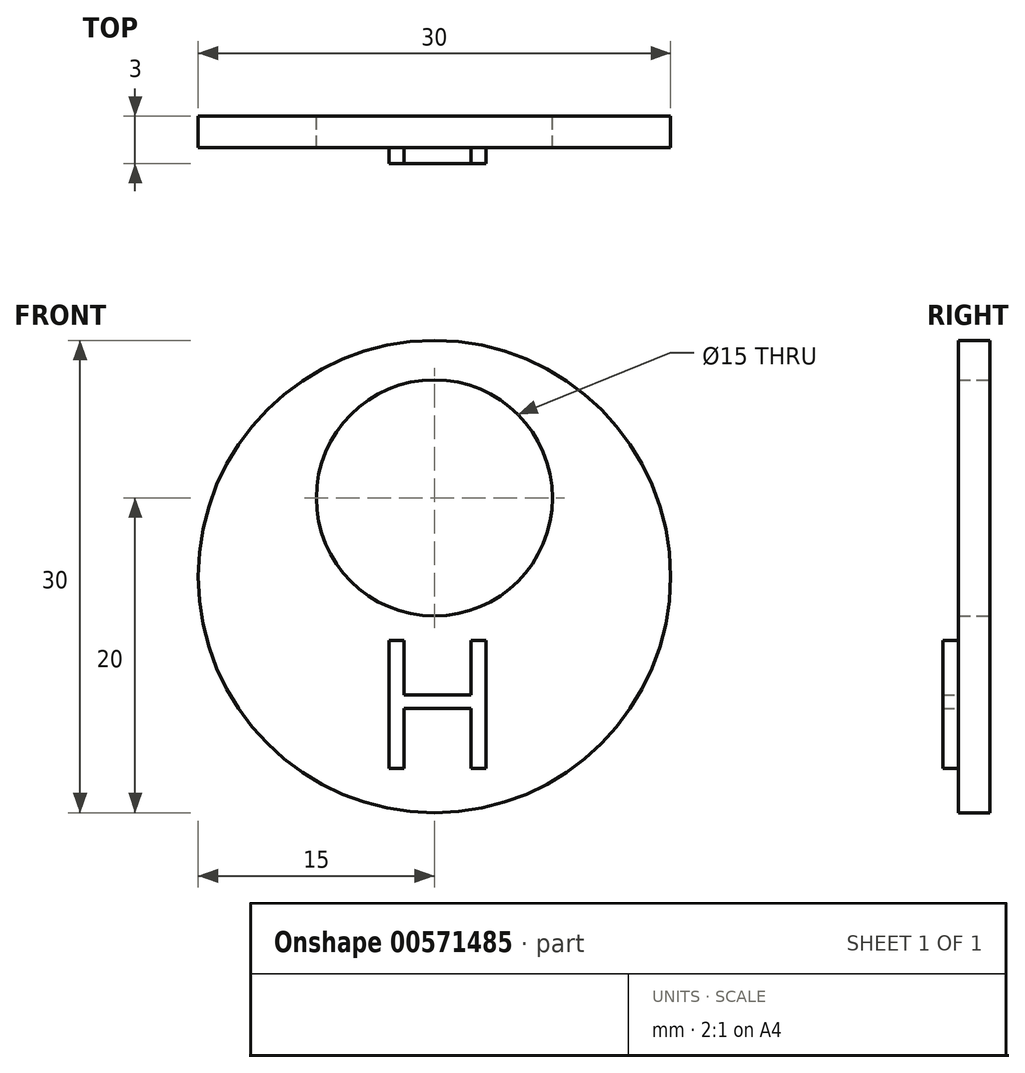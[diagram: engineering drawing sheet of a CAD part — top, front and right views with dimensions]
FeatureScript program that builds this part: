
annotation { "Feature Type Name" : "Feature", "Feature Type Description" : "" }
export const myFeature = defineFeature(function(context is Context, id is Id, definition is map)
    precondition{}
    {
        {
            var Q0;
            Q0=qCreatedBy(makeId("Front.planeOp"),FACE);
            var sketch = newSketch(context, id + "F0", { "sketchPlane" : qUnion([Q0])});
            skCircle(sketch, "E0", {"center": v(0, 0) * mm, "radius": 15 * mm});
            skPoint(sketch, "E1", {"position": v(0, 5) * mm});
            skCircle(sketch, "E2", {"center": v(0, 5) * mm, "radius": 7.5 * mm});
            skSolve(sketch);
        }
        {
            var Q0;
            Q0=makeQuery(id+"F0.imprint","IMPRINT",FACE,{"disambiguationData":[TD([[makeQuery(id+"F0.imprint","IMPRINT",EDGE,{"derivedFrom":sQuery(id+"F0.wireOp",EDGE,"E0")}),1.0]])]});
            extrude(context, id + "F1", {"entities" : qUnion([Q0]), "depth" : 2 * mm});
        }
        {
            var Q0;
            Q0=makeQuery(id+"F1.opExtrude","CAP_FACE",FACE,{"disambiguationData":[OSD([sQuery(id+"F0.wireOp",EDGE,"E0"),sQuery(id+"F0.wireOp",EDGE,"E2")])],"isStart":false});
            var sketch = newSketch(context, id + "F2", { "sketchPlane" : qUnion([Q0])});
            skText(sketch, "E3", { "text": "H", "fontName": "OpenSans-Regular.ttf"});
            const initialGuessF2  = {"E3": [-0.004, -0.01217, 1, 0, 0.00817]};
            skSetInitialGuess(sketch, initialGuessF2);
            skSolve(sketch);
        }
        {
            var Q0;
            Q0=qSketchRegion(id+"F2",true);
            extrude(context, id + "F3", {"entities" : qUnion([Q0]), "operationType" : NewBodyOperationType.ADD, "depth" : 1 * mm});
        }
    });
